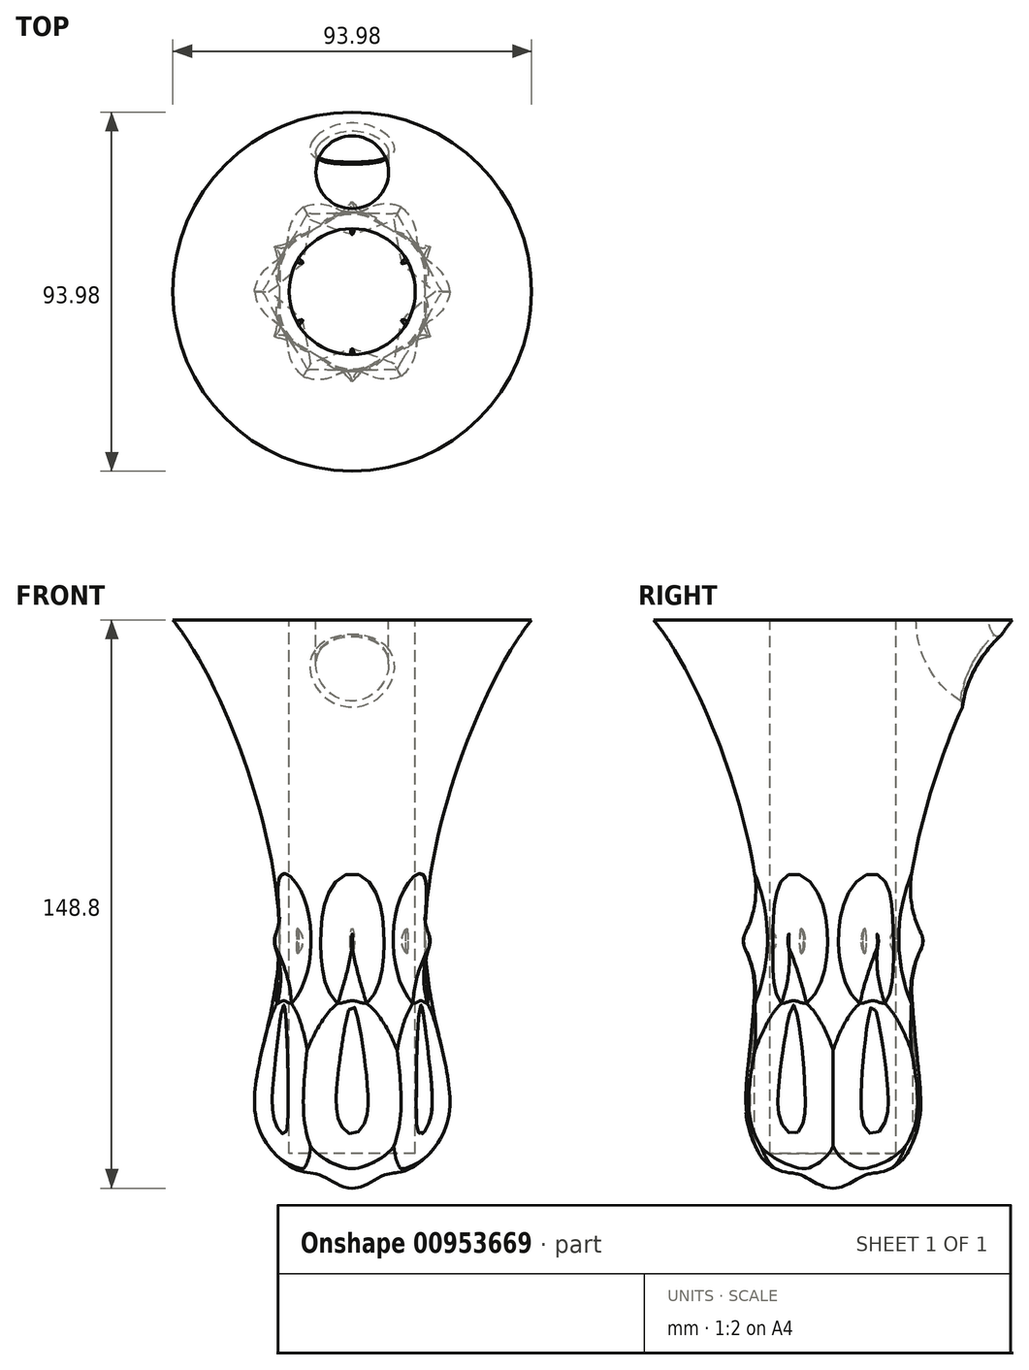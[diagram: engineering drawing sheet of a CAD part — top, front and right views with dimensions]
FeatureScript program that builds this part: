
annotation { "Feature Type Name" : "Feature", "Feature Type Description" : "" }
export const myFeature = defineFeature(function(context is Context, id is Id, definition is map)
    precondition{}
    {
        {
            var Q0;
            Q0=qCreatedBy(makeId("Front.planeOp"),FACE);
            var sketch = newSketch(context, id + "F0", { "sketchPlane" : qUnion([Q0])});
            skLineSegment(sketch, "E0", {"start": v(0, 0) * mm, "end": v(-16.51, 0) * mm});
            skLineSegment(sketch, "E1", {"start": v(-16.51, 0) * mm, "end": v(-16.51, 139.7) * mm});
            skLineSegment(sketch, "E2", {"start": v(-16.51, 139.7) * mm, "end": v(-47, 139.7) * mm});
            skPoint(sketch, "E3.4.internal.snap0", {"position": v(-8.26, 0) * mm});
            skFitSpline(sketch, "E3", {"points": [v(-47, 139.7) * mm, v(-19.1, 56.32) * mm, v(-25.28, 9.08) * mm, v(-14.37, -4.32) * mm, v(-8.26, -5.7) * mm, v(0, -9.1) * mm], "startDerivative": vector(103.36, -126) * mm, "endDerivative": vector(83.09, 0) * mm});
            skLineSegment(sketch, "E4", {"start": v(0, 0) * mm, "end": v(0, -9.1) * mm});
            skLineSegment(sketch, "E5", {"start": v(-47, 139.7) * mm, "end": v(-47, 131.83) * mm});
            skLineSegment(sketch, "E6", {"start": v(-41.53, 131.83) * mm, "end": v(-16.51, 131.83) * mm});
            skSolve(sketch);
        }
        {
            var Q0;
            Q0=qSketchRegion(id+"F0",true);
            var Q1;
            Q1=sQuery(id+"F0.wireOp",EDGE,"E4");
            revolve(context, id + "F1", {"surfaceOperationType" : NewSurfaceOperationType.NEW, "entities" : qUnion([Q0]), "axis" : qUnion([Q1]), "revolveType" : RevolveType.FULL});
        }
        {
            var Q0;
            Q0=qCreatedBy(makeId("Top.planeOp"),FACE);
            var sketch = newSketch(context, id + "F2", { "sketchPlane" : qUnion([Q0])});
            skCircle(sketch, "E7", {"center": v(0, -29.76) * mm, "radius": 9 * mm});
            skCircle(sketch, "E8.1.0", {"center": v(25.77, -14.88) * mm, "radius": 9 * mm});
            skCircle(sketch, "E8.2.0", {"center": v(25.77, 14.88) * mm, "radius": 9 * mm});
            skCircle(sketch, "E8.3.0", {"center": v(0, 29.76) * mm, "radius": 9 * mm});
            skCircle(sketch, "E8.4.0", {"center": v(-25.77, 14.88) * mm, "radius": 9 * mm});
            skCircle(sketch, "E8.5.0", {"center": v(-25.77, -14.88) * mm, "radius": 9 * mm});
            skPoint(sketch, "E8.center", {"position": v(0, 0) * mm});
            skSolve(sketch);
        }
        {
            var Q0;
            Q0=makeQuery(id+"F2.imprint","IMPRINT",FACE,{"disambiguationData":[TD([[makeQuery(id+"F2.imprint","IMPRINT",EDGE,{"derivedFrom":sQuery(id+"F2.wireOp",EDGE,"E7")}),1.0]])]});
            var Q1;
            Q1=makeQuery(id+"F2.imprint","IMPRINT",FACE,{"disambiguationData":[TD([[makeQuery(id+"F2.imprint","IMPRINT",EDGE,{"derivedFrom":sQuery(id+"F2.wireOp",EDGE,"E8.1.0")}),1.0]])]});
            var Q2;
            Q2=makeQuery(id+"F2.imprint","IMPRINT",FACE,{"disambiguationData":[TD([[makeQuery(id+"F2.imprint","IMPRINT",EDGE,{"derivedFrom":sQuery(id+"F2.wireOp",EDGE,"E8.5.0")}),1.0]])]});
            var Q3;
            Q3=makeQuery(id+"F2.imprint","IMPRINT",FACE,{"disambiguationData":[TD([[makeQuery(id+"F2.imprint","IMPRINT",EDGE,{"derivedFrom":sQuery(id+"F2.wireOp",EDGE,"E8.4.0")}),1.0]])]});
            var Q4;
            Q4=makeQuery(id+"F2.imprint","IMPRINT",FACE,{"disambiguationData":[TD([[makeQuery(id+"F2.imprint","IMPRINT",EDGE,{"derivedFrom":sQuery(id+"F2.wireOp",EDGE,"E8.2.0")}),1.0]])]});
            var Q5;
            Q5=makeQuery(id+"F2.imprint","IMPRINT",FACE,{"disambiguationData":[TD([[makeQuery(id+"F2.imprint","IMPRINT",EDGE,{"derivedFrom":sQuery(id+"F2.wireOp",EDGE,"E8.3.0")}),1.0]])]});
            extrude(context, id + "F3", {"entities" : qUnion([Q0, Q1, Q2, Q3, Q4, Q5]), "operationType" : NewBodyOperationType.REMOVE, "depth" : 54.1 * mm, "offsetDistance" : 25.4 * mm});
        }
        {
            var Q0;
            Q0=makeQuery(id+"F3.boolean.opBoolean","COPY",FACE,{"derivedFrom":makeQuery(id+"F3.opExtrude","SWEPT_FACE",FACE,{"disambiguationData":[OSD([sQuery(id+"F2.wireOp",EDGE,"E7")])]})});
            var Q1;
            Q1=makeQuery(id+"F3.boolean.opBoolean","COPY",FACE,{"derivedFrom":makeQuery(id+"F3.opExtrude","SWEPT_FACE",FACE,{"disambiguationData":[OSD([sQuery(id+"F2.wireOp",EDGE,"E8.1.0")])]})});
            var Q2;
            Q2=makeQuery(id+"F3.boolean.opBoolean","COPY",FACE,{"derivedFrom":makeQuery(id+"F3.opExtrude","SWEPT_FACE",FACE,{"disambiguationData":[OSD([sQuery(id+"F2.wireOp",EDGE,"E8.2.0")])]})});
            var Q3;
            Q3=makeQuery(id+"F3.boolean.opBoolean","INTERSECT",EDGE,{"derivedFrom":[makeQuery(id+"F1.opRevolve","SWEPT_FACE",FACE,{"disambiguationData":[OSD([sQuery(id+"F0.wireOp",EDGE,"E3")])]}),makeQuery(id+"F3.opExtrude","SWEPT_FACE",FACE,{"disambiguationData":[OSD([sQuery(id+"F2.wireOp",EDGE,"E8.3.0")])]})]});
            var Q4;
            Q4=makeQuery(id+"F3.boolean.opBoolean","COPY",FACE,{"derivedFrom":makeQuery(id+"F3.opExtrude","SWEPT_FACE",FACE,{"disambiguationData":[OSD([sQuery(id+"F2.wireOp",EDGE,"E8.4.0")])]})});
            var Q5;
            Q5=makeQuery(id+"F3.boolean.opBoolean","COPY",FACE,{"derivedFrom":makeQuery(id+"F3.opExtrude","SWEPT_FACE",FACE,{"disambiguationData":[OSD([sQuery(id+"F2.wireOp",EDGE,"E8.5.0")])]})});
            fillet(context, id + "F4", {"entities" : qUnion([Q0, Q1, Q2, Q3, Q4, Q5]), "radius" : 10.16 * mm, "tangentPropagation" : true, "allowEdgeOverflow" : false});
        }
        {
            var Q0;
            Q0=qCreatedBy(makeId("Top.planeOp"),FACE);
            cPlane(context, id + "F5", {"entities" : qUnion([Q0]), "cplaneType" : CPlaneType.OFFSET, "offset" : 55.63 * mm, "width" : 152.4 * mm, "height" : 152.4 * mm});
        }
        {
            var Q0;
            Q0=qCreatedBy(id+"F5.planeOp",FACE);
            var sketch = newSketch(context, id + "F6", { "sketchPlane" : qUnion([Q0])});
            skEllipse(sketch, "E9", {"center": v(0, -19.24) * mm, "majorRadius": 4.3 * mm, "minorRadius": 0.73 * mm, "majorAxis": v(0, -1)});
            skEllipse(sketch, "E10.1.0", {"center": v(16.67, -9.62) * mm, "majorRadius": 4.3 * mm, "minorRadius": 0.73 * mm, "majorAxis": v(0.87, -0.5)});
            skEllipse(sketch, "E10.2.0", {"center": v(16.67, 9.62) * mm, "majorRadius": 4.3 * mm, "minorRadius": 0.73 * mm, "majorAxis": v(0.87, 0.5)});
            skEllipse(sketch, "E10.3.0", {"center": v(0, 19.24) * mm, "majorRadius": 4.3 * mm, "minorRadius": 0.73 * mm, "majorAxis": v(0, 1)});
            skEllipse(sketch, "E10.4.0", {"center": v(-16.67, 9.62) * mm, "majorRadius": 4.3 * mm, "minorRadius": 0.73 * mm, "majorAxis": v(-0.87, 0.5)});
            skEllipse(sketch, "E10.5.0", {"center": v(-16.67, -9.62) * mm, "majorRadius": 4.3 * mm, "minorRadius": 0.73 * mm, "majorAxis": v(-0.87, -0.5)});
            skPoint(sketch, "E10.center", {"position": v(0, 0) * mm});
            skLineSegment(sketch, "E11", {"start": v(-16.67, -9.62) * mm, "end": v(-16.3, -10.25) * mm});
            skLineSegment(sketch, "E12", {"start": v(-16.67, -9.62) * mm, "end": v(-17.03, -9) * mm});
            skLineSegment(sketch, "E13", {"start": v(0, -19.24) * mm, "end": v(-0.73, -19.24) * mm});
            skLineSegment(sketch, "E14", {"start": v(0, -19.24) * mm, "end": v(0.73, -19.24) * mm});
            skLineSegment(sketch, "E15", {"start": v(16.67, -9.62) * mm, "end": v(16.3, -10.25) * mm});
            skLineSegment(sketch, "E16", {"start": v(16.67, -9.62) * mm, "end": v(17.03, -9) * mm});
            skLineSegment(sketch, "E17", {"start": v(16.67, 9.62) * mm, "end": v(17.03, 9) * mm});
            skLineSegment(sketch, "E18", {"start": v(16.67, 9.62) * mm, "end": v(16.3, 10.25) * mm});
            skLineSegment(sketch, "E19", {"start": v(0, 19.24) * mm, "end": v(-0.73, 19.24) * mm});
            skLineSegment(sketch, "E20", {"start": v(0, 19.24) * mm, "end": v(0.73, 19.24) * mm});
            skLineSegment(sketch, "E21", {"start": v(-16.67, 9.62) * mm, "end": v(-17.03, 9) * mm});
            skLineSegment(sketch, "E22", {"start": v(-16.67, 9.62) * mm, "end": v(-16.3, 10.25) * mm});
            skSolve(sketch);
        }
        {
            var Q0;
            {var subQ0=sQuery(id+"F6.wireOp",EDGE,"E11");Q0=makeQuery(id+"F6.imprint","IMPRINT",FACE,{"disambiguationData":[TD([[makeQuery(id+"F6.imprint","IMPRINT",EDGE,{"derivedFrom":subQ0}),-1.0]])]});}
            var Q1;
            Q1=sQuery(id+"F6.wireOp",EDGE,"E11");
            revolve(context, id + "F7", {"operationType" : NewBodyOperationType.ADD, "surfaceOperationType" : NewSurfaceOperationType.NEW, "entities" : qUnion([Q0]), "axis" : qUnion([Q1]), "revolveType" : RevolveType.FULL});
        }
        {
            var Q0;
            {var subQ0=sQuery(id+"F6.wireOp",EDGE,"E13");Q0=makeQuery(id+"F6.imprint","IMPRINT",FACE,{"disambiguationData":[TD([[makeQuery(id+"F6.imprint","IMPRINT",EDGE,{"derivedFrom":subQ0}),1.0]])]});}
            var Q1;
            Q1=sQuery(id+"F6.wireOp",EDGE,"E14");
            revolve(context, id + "F8", {"operationType" : NewBodyOperationType.ADD, "surfaceOperationType" : NewSurfaceOperationType.NEW, "entities" : qUnion([Q0]), "axis" : qUnion([Q1]), "revolveType" : RevolveType.FULL});
        }
        {
            var Q0;
            {var subQ0=sQuery(id+"F6.wireOp",EDGE,"E15");Q0=makeQuery(id+"F6.imprint","IMPRINT",FACE,{"disambiguationData":[TD([[makeQuery(id+"F6.imprint","IMPRINT",EDGE,{"derivedFrom":subQ0}),-1.0]])]});}
            var Q1;
            Q1=sQuery(id+"F6.wireOp",EDGE,"E15");
            revolve(context, id + "F9", {"operationType" : NewBodyOperationType.ADD, "surfaceOperationType" : NewSurfaceOperationType.NEW, "entities" : qUnion([Q0]), "axis" : qUnion([Q1]), "revolveType" : RevolveType.FULL});
        }
        {
            var Q0;
            {var subQ0=sQuery(id+"F6.wireOp",EDGE,"E17");Q0=makeQuery(id+"F6.imprint","IMPRINT",FACE,{"disambiguationData":[TD([[makeQuery(id+"F6.imprint","IMPRINT",EDGE,{"derivedFrom":subQ0}),-1.0]])]});}
            var Q1;
            Q1=sQuery(id+"F6.wireOp",EDGE,"E18");
            revolve(context, id + "F10", {"operationType" : NewBodyOperationType.ADD, "surfaceOperationType" : NewSurfaceOperationType.NEW, "entities" : qUnion([Q0]), "axis" : qUnion([Q1]), "revolveType" : RevolveType.FULL});
        }
        {
            var Q0;
            {var subQ0=sQuery(id+"F6.wireOp",EDGE,"E19");Q0=makeQuery(id+"F6.imprint","IMPRINT",FACE,{"disambiguationData":[TD([[makeQuery(id+"F6.imprint","IMPRINT",EDGE,{"derivedFrom":subQ0}),1.0]])]});}
            var Q1;
            Q1=sQuery(id+"F6.wireOp",EDGE,"E19");
            revolve(context, id + "F11", {"operationType" : NewBodyOperationType.ADD, "surfaceOperationType" : NewSurfaceOperationType.NEW, "entities" : qUnion([Q0]), "axis" : qUnion([Q1]), "revolveType" : RevolveType.FULL});
        }
        {
            var Q0;
            {var subQ0=sQuery(id+"F6.wireOp",EDGE,"E21");Q0=makeQuery(id+"F6.imprint","IMPRINT",FACE,{"disambiguationData":[TD([[makeQuery(id+"F6.imprint","IMPRINT",EDGE,{"derivedFrom":subQ0}),1.0]])]});}
            var Q1;
            Q1=sQuery(id+"F6.wireOp",EDGE,"E22");
            revolve(context, id + "F12", {"operationType" : NewBodyOperationType.ADD, "surfaceOperationType" : NewSurfaceOperationType.NEW, "entities" : qUnion([Q0]), "axis" : qUnion([Q1]), "revolveType" : RevolveType.FULL});
        }
        {
            var Q0;
            Q0=makeQuery(id+"F7.boolean.opBoolean","INTERSECT",EDGE,{"derivedFrom":[makeQuery(id+"F4.opFillet","SPLIT",FACE,{"disambiguationData":[OD(1.0)],"derivedFrom":makeQuery(id+"F1.opRevolve","SWEPT_FACE",FACE,{"disambiguationData":[OSD([sQuery(id+"F0.wireOp",EDGE,"E3")])]})}),makeQuery(id+"F7.opRevolve","SWEPT_FACE",FACE,{"disambiguationData":[OSD([sQuery(id+"F6.wireOp",EDGE,"E10.5.0")])]})]});
            var Q1;
            Q1=makeQuery(id+"F8.boolean.opBoolean","INTERSECT",EDGE,{"derivedFrom":[makeQuery(id+"F4.opFillet","SPLIT",FACE,{"disambiguationData":[OD(1.0)],"derivedFrom":makeQuery(id+"F1.opRevolve","SWEPT_FACE",FACE,{"disambiguationData":[OSD([sQuery(id+"F0.wireOp",EDGE,"E3")])]})}),makeQuery(id+"F8.opRevolve","SWEPT_FACE",FACE,{"disambiguationData":[OSD([sQuery(id+"F6.wireOp",EDGE,"E9")])]})]});
            var Q2;
            Q2=makeQuery(id+"F9.boolean.opBoolean","INTERSECT",EDGE,{"derivedFrom":[makeQuery(id+"F4.opFillet","SPLIT",FACE,{"disambiguationData":[OD(1.0)],"derivedFrom":makeQuery(id+"F1.opRevolve","SWEPT_FACE",FACE,{"disambiguationData":[OSD([sQuery(id+"F0.wireOp",EDGE,"E3")])]})}),makeQuery(id+"F9.opRevolve","SWEPT_FACE",FACE,{"disambiguationData":[OSD([sQuery(id+"F6.wireOp",EDGE,"E10.1.0")])]})]});
            var Q3;
            Q3=makeQuery(id+"F10.boolean.opBoolean","INTERSECT",EDGE,{"derivedFrom":[makeQuery(id+"F4.opFillet","SPLIT",FACE,{"disambiguationData":[OD(1.0)],"derivedFrom":makeQuery(id+"F1.opRevolve","SWEPT_FACE",FACE,{"disambiguationData":[OSD([sQuery(id+"F0.wireOp",EDGE,"E3")])]})}),makeQuery(id+"F10.opRevolve","SWEPT_FACE",FACE,{"disambiguationData":[OSD([sQuery(id+"F6.wireOp",EDGE,"E10.2.0")])]})]});
            var Q4;
            Q4=makeQuery(id+"F11.boolean.opBoolean","INTERSECT",EDGE,{"derivedFrom":[makeQuery(id+"F4.opFillet","SPLIT",FACE,{"disambiguationData":[OD(1.0)],"derivedFrom":makeQuery(id+"F1.opRevolve","SWEPT_FACE",FACE,{"disambiguationData":[OSD([sQuery(id+"F0.wireOp",EDGE,"E3")])]})}),makeQuery(id+"F11.opRevolve","SWEPT_FACE",FACE,{"disambiguationData":[OSD([sQuery(id+"F6.wireOp",EDGE,"E10.3.0")])]})]});
            var Q5;
            Q5=makeQuery(id+"F12.boolean.opBoolean","INTERSECT",EDGE,{"derivedFrom":[makeQuery(id+"F4.opFillet","SPLIT",FACE,{"disambiguationData":[OD(1.0)],"derivedFrom":makeQuery(id+"F1.opRevolve","SWEPT_FACE",FACE,{"disambiguationData":[OSD([sQuery(id+"F0.wireOp",EDGE,"E3")])]})}),makeQuery(id+"F12.opRevolve","SWEPT_FACE",FACE,{"disambiguationData":[OSD([sQuery(id+"F6.wireOp",EDGE,"E10.4.0")])]})]});
            fillet(context, id + "F13", {"entities" : qUnion([Q0, Q1, Q2, Q3, Q4, Q5]), "radius" : 25.4 * mm, "tangentPropagation" : true, "allowEdgeOverflow" : false});
        }
        {
            var Q0;
            Q0=makeQuery(id+"F1.opRevolve","SWEPT_FACE",FACE,{"disambiguationData":[OSD([sQuery(id+"F0.wireOp",EDGE,"E2")])]});
            var sketch = newSketch(context, id + "F14", { "sketchPlane" : qUnion([Q0])});
            skLineSegment(sketch, "E23", {"start": v(0, 47) * mm, "end": v(0, 0) * mm});
            skLineSegment(sketch, "E24", {"start": v(0, -0.48) * mm, "end": v(0, 31.27) * mm});
            skCircle(sketch, "E25", {"center": v(0, 31.27) * mm, "radius": 9.53 * mm});
            skLineSegment(sketch, "E26", {"start": v(0, 47) * mm, "end": v(-12.82, 47) * mm});
            skSolve(sketch);
        }
        {
            var Q0;
            {var subQ0=sQuery(id+"F14.wireOp",EDGE,"E24");var subQ1=sQuery(id+"F14.wireOp",EDGE,"E23");var subQ2=makeQuery(id+"F14.imprint","INTERSECT",VERTEX,{"derivedFrom":[subQ1,subQ0]});Q0=makeQuery(id+"F14.imprint","IMPRINT",FACE,{"disambiguationData":[TD([[makeQuery(id+"F14.imprint","IMPRINT",EDGE,{"disambiguationData":[TD([[subQ2,1.0]])],"derivedFrom":subQ1}),-1.0]])]});}
            var Q1;
            {var subQ0=sQuery(id+"F14.wireOp",EDGE,"E24");var subQ1=sQuery(id+"F14.wireOp",EDGE,"E23");var subQ2=makeQuery(id+"F14.imprint","INTERSECT",VERTEX,{"derivedFrom":[subQ1,subQ0]});Q1=makeQuery(id+"F14.imprint","IMPRINT",FACE,{"disambiguationData":[TD([[makeQuery(id+"F14.imprint","IMPRINT",EDGE,{"disambiguationData":[TD([[subQ2,1.0]])],"derivedFrom":subQ1}),1.0]])]});}
            var Q2;
            Q2=sQuery(id+"F14.wireOp",EDGE,"E26");
            revolve(context, id + "F15", {"operationType" : NewBodyOperationType.REMOVE, "surfaceOperationType" : NewSurfaceOperationType.NEW, "entities" : qUnion([Q0, Q1]), "axis" : qUnion([Q2]), "revolveType" : RevolveType.FULL, "oppositeDirection" : true});
        }
        {
            var Q0;
            Q0=makeQuery(id+"F15.boolean.opBoolean","INTERSECT",EDGE,{"derivedFrom":[makeQuery(id+"F4.opFillet","SPLIT",FACE,{"disambiguationData":[OD(1.0)],"derivedFrom":makeQuery(id+"F1.opRevolve","SWEPT_FACE",FACE,{"disambiguationData":[OSD([sQuery(id+"F0.wireOp",EDGE,"E3")])]})}),makeQuery(id+"F15.opRevolve","SWEPT_FACE",FACE,{"disambiguationData":[OSD([sQuery(id+"F14.wireOp",EDGE,"E25")])]})]});
            fillet(context, id + "F16", {"entities" : qUnion([Q0]), "radius" : 1.27 * mm, "tangentPropagation" : true, "allowEdgeOverflow" : false});
        }
    });
